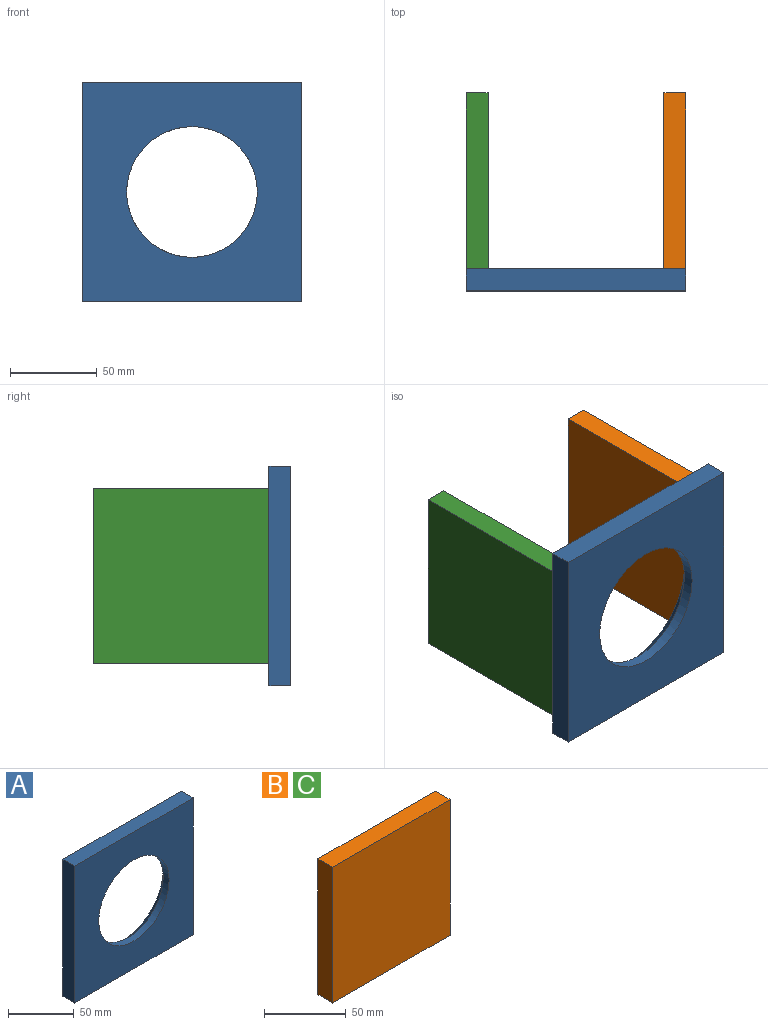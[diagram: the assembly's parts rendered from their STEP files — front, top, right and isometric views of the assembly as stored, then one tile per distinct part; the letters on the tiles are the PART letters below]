
ASSEMBLY  parts=3 mates=2
PART A: 8 faces, bbox 127x12.7x127 mm
  f0: plane 127x12.7mm, normal (-1,0,0), area 1612.9mm2, adj f1,f4,f5,f6
  f1: plane 127x12.7mm, normal (0,0,-1), area 1612.9mm2, adj f0,f2,f5,f6
  f2: plane 127x12.7mm, normal (1,0,0), area 1612.9mm2, adj f1,f4,f5,f6
  f3: cylinder r=37.72mm len=75.44mm, axis (0,1,0), area 1504.9mm2, adj f5,f7
  f4: plane 127x12.7mm, normal (0,0,1), area 1612.9mm2, adj f0,f2,f5,f6
  f5: plane 127x127mm, normal (0,-1,0), area 11659.4mm2, adj f0,f1,f2,f3,f4
  f6: plane 127x127mm, normal (0,1,0), area 10027.8mm2, adj f0,f1,f2,f4,f7
  f7: cone r=44.07mm half-angle=45deg, axis (0,1,0), area 2307.4mm2, adj f3,f6
PART B: 6 faces, bbox 101.6x12.7x101.6 mm
  f0: plane 101.6x12.7mm, normal (-1,0,0), area 1290.3mm2, adj f1,f3,f4,f5
  f1: plane 101.6x12.7mm, normal (0,0,-1), area 1290.3mm2, adj f0,f2,f4,f5
  f2: plane 101.6x12.7mm, normal (1,0,0), area 1290.3mm2, adj f1,f3,f4,f5
  f3: plane 101.6x12.7mm, normal (0,0,1), area 1290.3mm2, adj f0,f2,f4,f5
  f4: plane 101.6x101.6mm, normal (0,-1,0), area 10322.6mm2, adj f0,f1,f2,f3
  f5: plane 101.6x101.6mm, normal (0,1,0), area 10322.6mm2, adj f0,f1,f2,f3
PART C: same geometry as B
PLACE A t=(3.58,5.28,-1.27)mm fixed
PLACE B rot(axis=(0,0,1),90deg) t=(54.38,56.08,-1.27)mm
PLACE C rot(axis=(0,0,1),90deg) t=(-59.92,56.08,-1.27)mm
MATE fastened B.f0 <-> A.f6  axis (0,-1,0) through (60.73,5.28,-1.27)mm
MATE fastened A.f6 <-> C.f0  axis (0,1,0) through (-59.92,5.28,-1.27)mm
